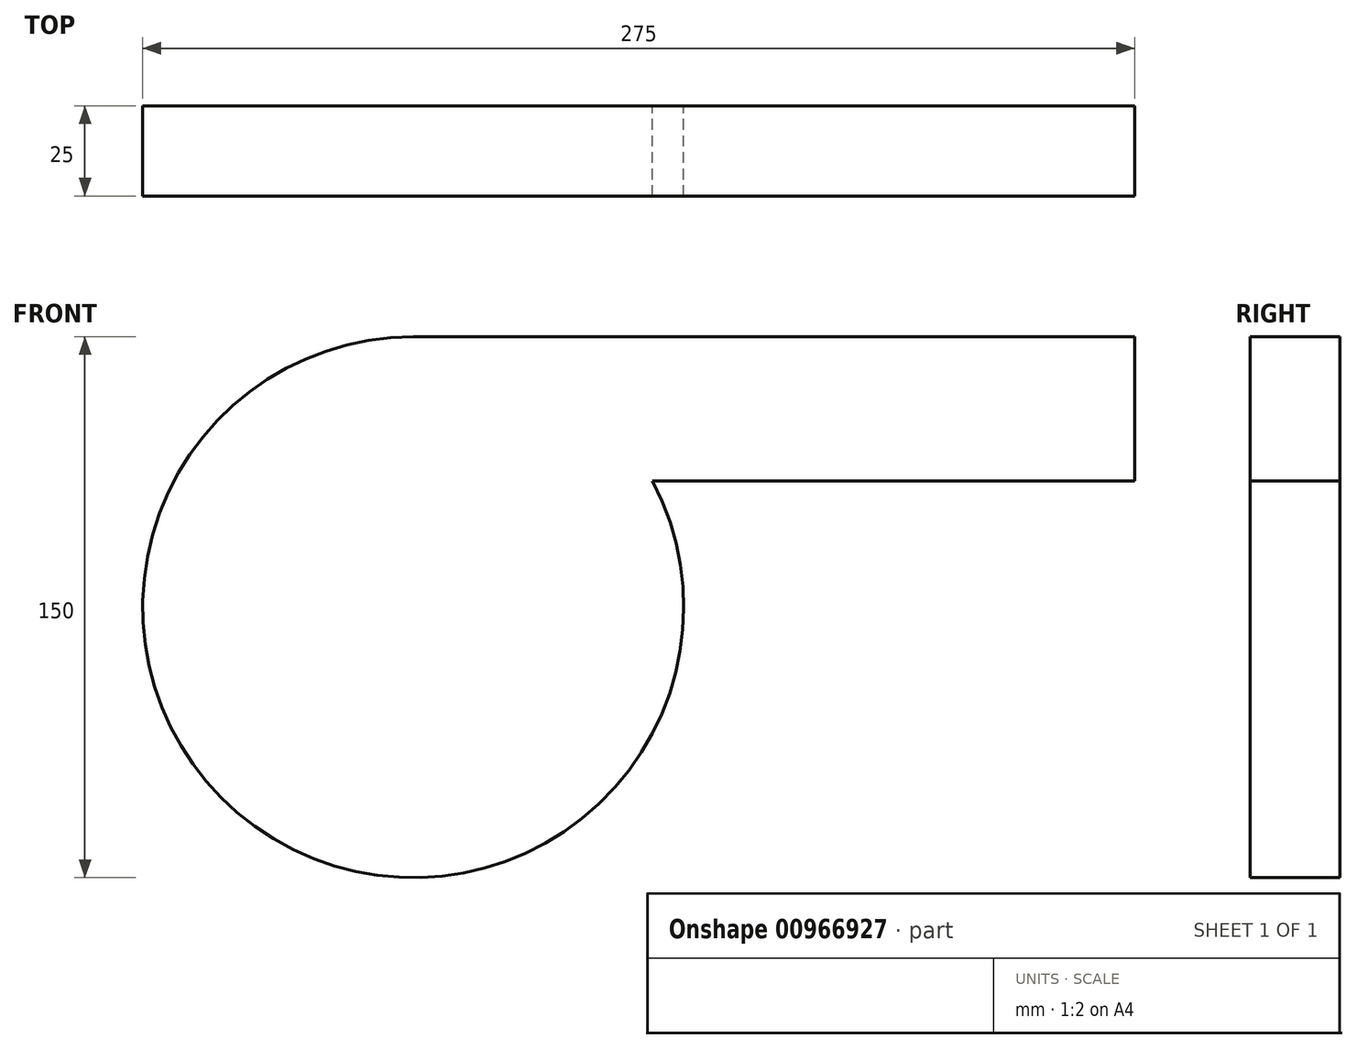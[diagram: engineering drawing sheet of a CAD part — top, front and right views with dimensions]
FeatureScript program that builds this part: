
annotation { "Feature Type Name" : "Feature", "Feature Type Description" : "" }
export const myFeature = defineFeature(function(context is Context, id is Id, definition is map)
    precondition{}
    {
        {
            var Q0;
            Q0=qCreatedBy(makeId("Front.planeOp"),FACE);
            var sketch = newSketch(context, id + "F0", { "sketchPlane" : qUnion([Q0])});
            skLineSegment(sketch, "E0", {"start": v(0, 0) * mm, "end": v(-200, 0) * mm, "construction": true});
            skArc(sketch, "E1", {"start": v(-200, 75) * mm, "mid": v(-238.73, -64.23) * mm, "end": v(-133.67, 35) * mm});
            skLineSegment(sketch, "E2", {"start": v(-200, 75) * mm, "end": v(0, 75) * mm});
            skLineSegment(sketch, "E3", {"start": v(0, 75) * mm, "end": v(0, 35) * mm});
            skLineSegment(sketch, "E4", {"start": v(0, 35) * mm, "end": v(-133.67, 35) * mm});
            skSolve(sketch);
        }
        {
            var Q0;
            Q0 = qSketchRegion(id + "F0", true);
            extrude(context, id + "F1", {"entities" : qUnion([Q0]), "depth" : 25 * mm, "offsetDistance" : 25 * mm});
        }
    });
